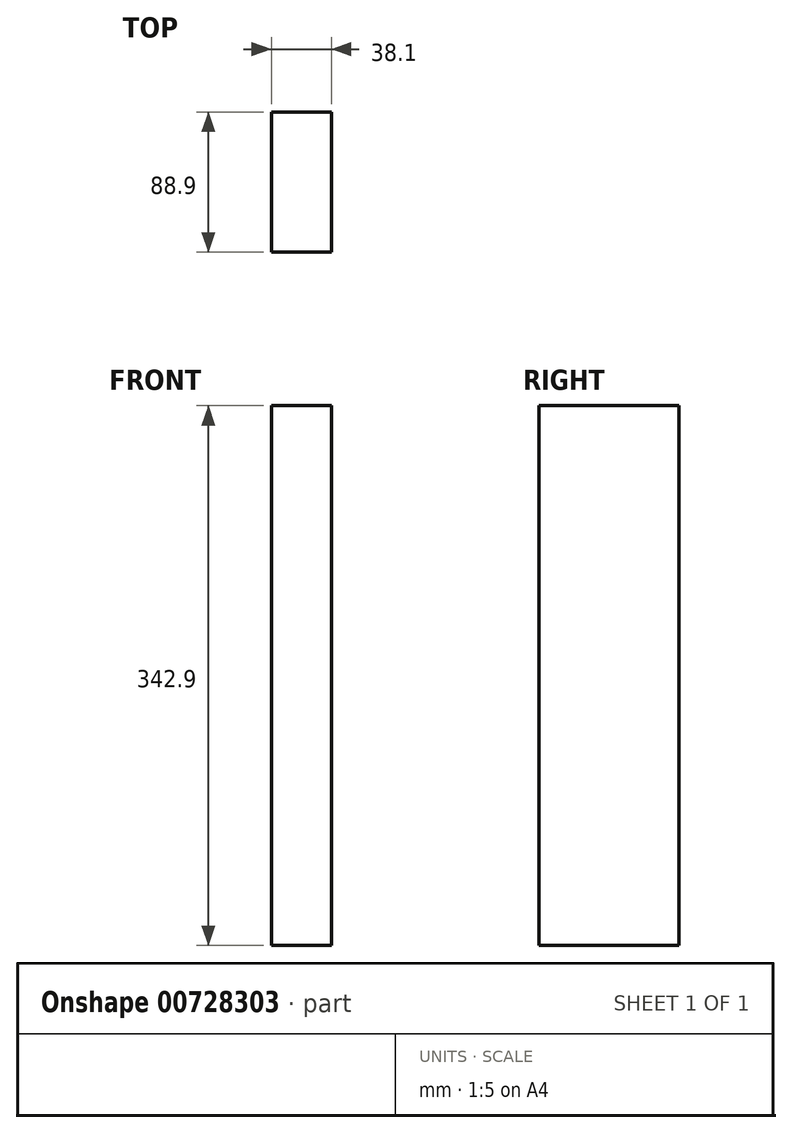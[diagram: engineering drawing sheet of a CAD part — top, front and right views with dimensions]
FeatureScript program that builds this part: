
annotation { "Feature Type Name" : "Feature", "Feature Type Description" : "" }
export const myFeature = defineFeature(function(context is Context, id is Id, definition is map)
    precondition{}
    {
        {
            var Q0;
            Q0=qCreatedBy(makeId("Front.planeOp"),FACE);
            var sketch = newSketch(context, id + "F0", { "sketchPlane" : qUnion([Q0])});
            skLineSegment(sketch, "E0.bottom", {"start": v(19.05, -171.45) * mm, "end": v(-19.05, -171.45) * mm});
            skLineSegment(sketch, "E0.top", {"start": v(19.05, 171.45) * mm, "end": v(-19.05, 171.45) * mm});
            skLineSegment(sketch, "E0.left", {"start": v(19.05, -171.45) * mm, "end": v(19.05, 171.45) * mm});
            skLineSegment(sketch, "E0.right", {"start": v(-19.05, -171.45) * mm, "end": v(-19.05, 171.45) * mm});
            skPoint(sketch, "E0.middle", {"position": v(0, 0) * mm});
            skSolve(sketch);
        }
        {
            var Q0;
            Q0=qSketchRegion(id+"F0",true);
            extrude(context, id + "F1", {"entities" : qUnion([Q0]), "depth" : 88.9 * mm, "offsetDistance" : 25.4 * mm});
        }
    });
